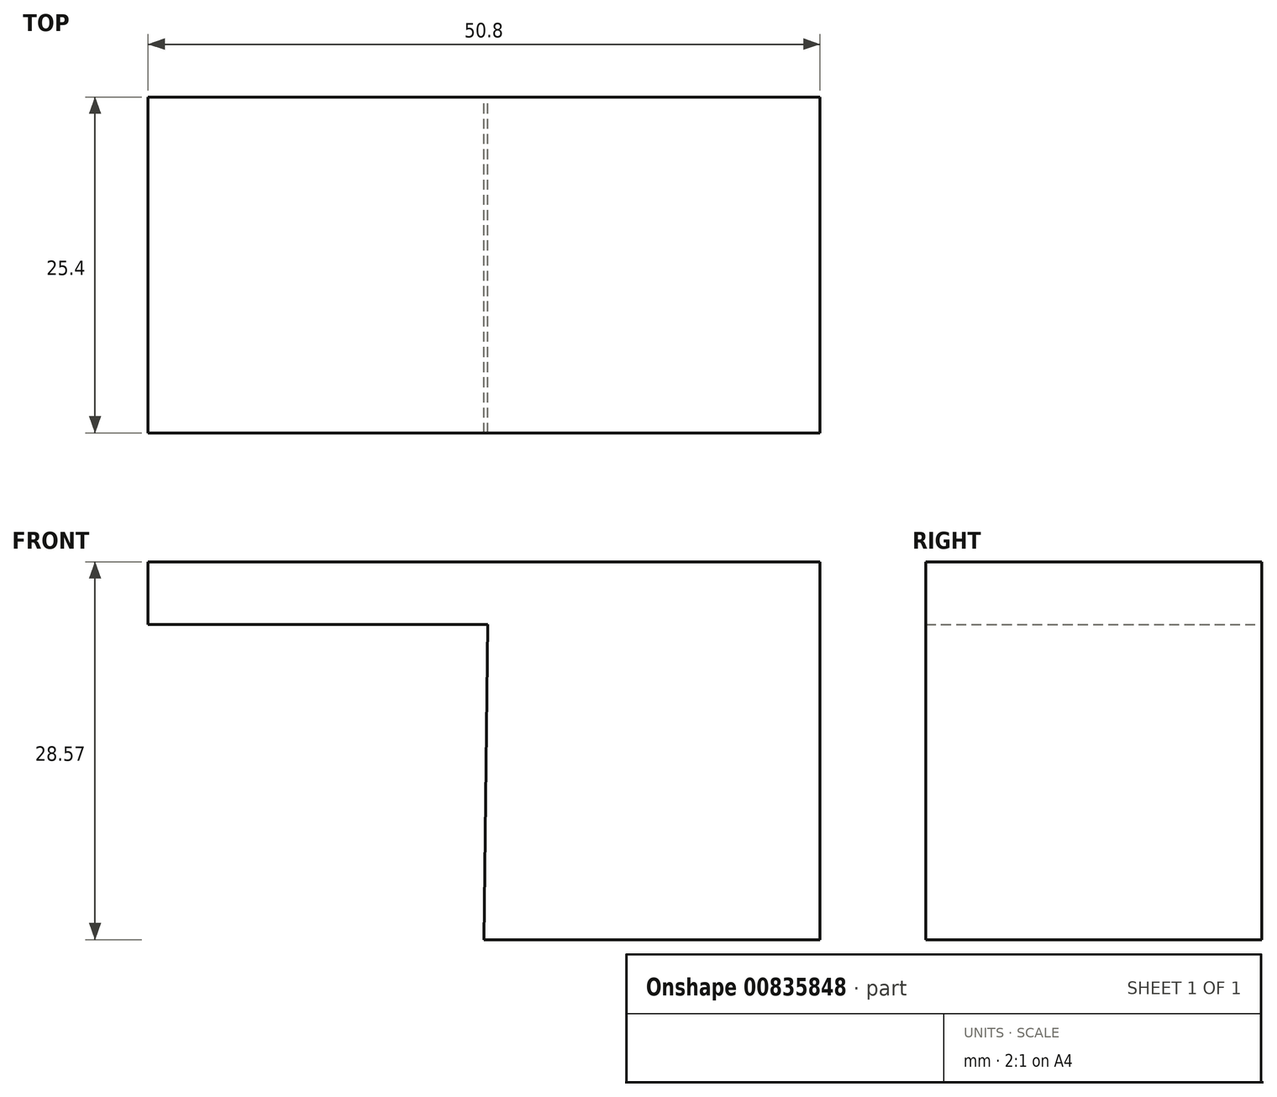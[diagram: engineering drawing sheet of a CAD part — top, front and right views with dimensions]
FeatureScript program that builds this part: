
annotation { "Feature Type Name" : "Feature", "Feature Type Description" : "" }
export const myFeature = defineFeature(function(context is Context, id is Id, definition is map)
    precondition{}
    {
        {
            var Q0;
            Q0=qCreatedBy(makeId("Front.planeOp"),FACE);
            var sketch = newSketch(context, id + "F0", { "sketchPlane" : qUnion([Q0])});
            skLineSegment(sketch, "E0.bottom", {"start": v(41.28, -9.52) * mm, "end": v(-41.28, -9.53) * mm});
            skLineSegment(sketch, "E0.top", {"start": v(41.27, 9.53) * mm, "end": v(-41.28, 9.53) * mm});
            skLineSegment(sketch, "E0.left", {"start": v(41.28, -9.52) * mm, "end": v(41.27, 9.53) * mm});
            skLineSegment(sketch, "E0.right", {"start": v(-41.27, -9.53) * mm, "end": v(-41.28, 9.52) * mm});
            skPoint(sketch, "E0.middle", {"position": v(0, 0) * mm});
            skLineSegment(sketch, "E1.bottom", {"start": v(111.12, 38.1) * mm, "end": v(60.32, 38.1) * mm});
            skLineSegment(sketch, "E1.top", {"start": v(111.12, 66.68) * mm, "end": v(60.32, 66.68) * mm});
            skLineSegment(sketch, "E1.left", {"start": v(111.12, 38.1) * mm, "end": v(111.12, 66.68) * mm});
            skLineSegment(sketch, "E1.right", {"start": v(60.32, 38.1) * mm, "end": v(60.32, 66.68) * mm});
            skPoint(sketch, "E1.middle", {"position": v(85.72, 52.39) * mm});
            skLineSegment(sketch, "E2", {"start": v(41.27, 9.53) * mm, "end": v(41.27, 31.84) * mm});
            skArc(sketch, "E3", {"start": v(41.27, 31.84) * mm, "mid": v(44.5, 39.64) * mm, "end": v(52.3, 42.88) * mm});
            skLineSegment(sketch, "E4", {"start": v(52.3, 42.88) * mm, "end": v(86, 42.88) * mm});
            skLineSegment(sketch, "E5.0", {"start": v(52.3, 61.93) * mm, "end": v(86, 61.93) * mm});
            skArc(sketch, "E5.1", {"start": v(22.22, 31.84) * mm, "mid": v(31.04, 53.11) * mm, "end": v(52.3, 61.93) * mm});
            skLineSegment(sketch, "E5.2", {"start": v(22.22, 9.53) * mm, "end": v(22.22, 31.84) * mm});
            skLineSegment(sketch, "E6", {"start": v(85.72, 38.1) * mm, "end": v(86, 61.93) * mm});
            skFitSpline(sketch, "E7", {"points": [v(-41.28, 9.52) * mm, v(52.3, 61.93) * mm], "startDerivative": vector(4.7, 86.87) * mm, "endDerivative": vector(137.7, -23.06) * mm});
            skSolve(sketch);
        }
        {
            var Q0;
            {var subQ1=sQuery(id+"F0.wireOp",EDGE,"E1.top");Q0=makeQuery(id+"F0.imprint","IMPRINT",FACE,{"disambiguationData":[TD([[makeQuery(id+"F0.imprint","IMPRINT",EDGE,{"derivedFrom":subQ1}),1.0]])]});}
            extrude(context, id + "F1", {"entities" : qUnion([Q0]), "depth" : 25.4 * mm, "offsetDistance" : 25.4 * mm});
        }
    });
